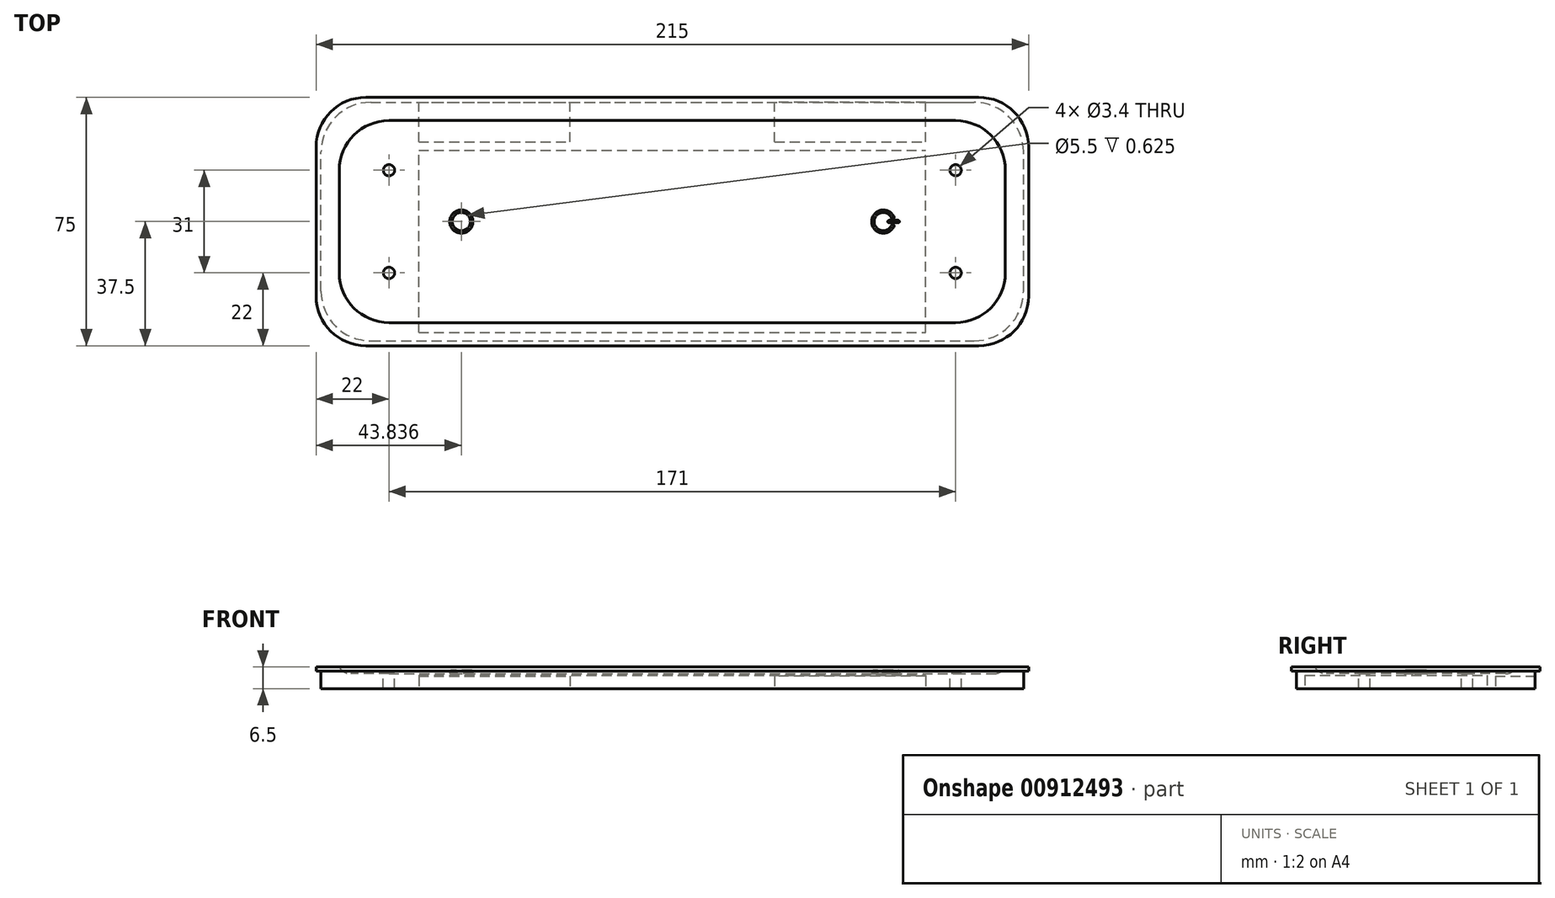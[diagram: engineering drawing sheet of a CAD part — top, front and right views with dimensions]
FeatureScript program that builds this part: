
annotation { "Feature Type Name" : "Feature", "Feature Type Description" : "" }
export const myFeature = defineFeature(function(context is Context, id is Id, definition is map)
    precondition{}
    {
        {
            var Q0;
            Q0=qCreatedBy(makeId("Top.planeOp"),FACE);
            var sketch = newSketch(context, id + "F0", { "sketchPlane" : qUnion([Q0])});
            skLineSegment(sketch, "E0.bottom", {"start": v(-107.5, 37.5) * mm, "end": v(107.5, 37.5) * mm});
            skLineSegment(sketch, "E0.top", {"start": v(-107.5, -37.5) * mm, "end": v(107.5, -37.5) * mm});
            skLineSegment(sketch, "E0.left", {"start": v(-107.5, 37.5) * mm, "end": v(-107.5, -37.5) * mm});
            skLineSegment(sketch, "E0.right", {"start": v(107.5, 37.5) * mm, "end": v(107.5, -37.5) * mm});
            skPoint(sketch, "E0.middle", {"position": v(0, 0) * mm});
            skSolve(sketch);
        }
        {
            var Q0;
            Q0=qSketchRegion(id+"F0",true);
            extrude(context, id + "F1", {"entities" : qUnion([Q0]), "depth" : 1.25 * mm, "offsetDistance" : 25 * mm});
        }
        {
            var Q0;
            Q0=makeQuery(id+"F1.opExtrude","SWEPT_EDGE",EDGE,{"disambiguationData":[OSD([sQuery(id+"F0.wireOp",EDGE,"E0.top"),sQuery(id+"F0.wireOp",EDGE,"E0.right")])]});
            var Q1;
            Q1=makeQuery(id+"F1.opExtrude","SWEPT_EDGE",EDGE,{"disambiguationData":[OSD([sQuery(id+"F0.wireOp",EDGE,"E0.bottom"),sQuery(id+"F0.wireOp",EDGE,"E0.right")])]});
            var Q2;
            Q2=makeQuery(id+"F1.opExtrude","SWEPT_EDGE",EDGE,{"disambiguationData":[OSD([sQuery(id+"F0.wireOp",EDGE,"E0.bottom"),sQuery(id+"F0.wireOp",EDGE,"E0.left")])]});
            var Q3;
            Q3=makeQuery(id+"F1.opExtrude","SWEPT_EDGE",EDGE,{"disambiguationData":[OSD([sQuery(id+"F0.wireOp",EDGE,"E0.top"),sQuery(id+"F0.wireOp",EDGE,"E0.left")])]});
            fillet(context, id + "F2", {"entities" : qUnion([Q0, Q1, Q2, Q3]), "radius" : 15 * mm, "tangentPropagation" : true, "allowEdgeOverflow" : false});
        }
        {
            var Q0;
            Q0=makeQuery(id+"F1.opExtrude","CAP_FACE",FACE,{"disambiguationData":[OSD([sQuery(id+"F0.wireOp",EDGE,"E0.bottom"),sQuery(id+"F0.wireOp",EDGE,"E0.top"),sQuery(id+"F0.wireOp",EDGE,"E0.left"),sQuery(id+"F0.wireOp",EDGE,"E0.right")])],"isStart":true});
            var sketch = newSketch(context, id + "F3", { "sketchPlane" : qUnion([Q0])});
            skLineSegment(sketch, "E1.bottom", {"start": v(-106, 36) * mm, "end": v(106, 36) * mm});
            skLineSegment(sketch, "E1.top", {"start": v(-106, -36) * mm, "end": v(106, -36) * mm});
            skLineSegment(sketch, "E1.left", {"start": v(-106, 36) * mm, "end": v(-106, -36) * mm});
            skLineSegment(sketch, "E1.right", {"start": v(106, 36) * mm, "end": v(106, -36) * mm});
            skPoint(sketch, "E1.middle", {"position": v(0, 0) * mm});
            skSolve(sketch);
        }
        {
            var Q0;
            Q0=qSketchRegion(id+"F3",true);
            extrude(context, id + "F4", {"entities" : qUnion([Q0]), "operationType" : NewBodyOperationType.ADD, "depth" : 5.25 * mm, "offsetDistance" : 25 * mm});
        }
        {
            var Q0;
            Q0=makeQuery(id+"F4.opExtrude","SWEPT_EDGE",EDGE,{"disambiguationData":[OSD([sQuery(id+"F3.wireOp",EDGE,"E1.bottom"),sQuery(id+"F3.wireOp",EDGE,"E1.left")])]});
            var Q1;
            Q1=makeQuery(id+"F4.opExtrude","SWEPT_EDGE",EDGE,{"disambiguationData":[OSD([sQuery(id+"F3.wireOp",EDGE,"E1.top"),sQuery(id+"F3.wireOp",EDGE,"E1.left")])]});
            var Q2;
            Q2=makeQuery(id+"F4.opExtrude","SWEPT_EDGE",EDGE,{"disambiguationData":[OSD([sQuery(id+"F3.wireOp",EDGE,"E1.top"),sQuery(id+"F3.wireOp",EDGE,"E1.right")])]});
            var Q3;
            Q3=makeQuery(id+"F4.opExtrude","SWEPT_EDGE",EDGE,{"disambiguationData":[OSD([sQuery(id+"F3.wireOp",EDGE,"E1.bottom"),sQuery(id+"F3.wireOp",EDGE,"E1.right")])]});
            fillet(context, id + "F5", {"entities" : qUnion([Q0, Q1, Q2, Q3]), "radius" : 15 * mm, "tangentPropagation" : true, "allowEdgeOverflow" : false});
        }
        {
            var Q0;
            Q0=makeQuery(id+"F1.opExtrude","CAP_FACE",FACE,{"disambiguationData":[OSD([sQuery(id+"F0.wireOp",EDGE,"E0.bottom"),sQuery(id+"F0.wireOp",EDGE,"E0.top"),sQuery(id+"F0.wireOp",EDGE,"E0.left"),sQuery(id+"F0.wireOp",EDGE,"E0.right")])],"isStart":false});
            var sketch = newSketch(context, id + "F6", { "sketchPlane" : qUnion([Q0])});
            skLineSegment(sketch, "E2.bottom", {"start": v(-106, 36) * mm, "end": v(106, 36) * mm});
            skLineSegment(sketch, "E2.top", {"start": v(-106, -36) * mm, "end": v(106, -36) * mm});
            skLineSegment(sketch, "E2.left", {"start": v(-106, 36) * mm, "end": v(-106, -36) * mm});
            skLineSegment(sketch, "E2.right", {"start": v(106, 36) * mm, "end": v(106, -36) * mm});
            skPoint(sketch, "E2.middle", {"position": v(0, 0) * mm});
            skSolve(sketch);
        }
        {
            var Q0;
            Q0=makeQuery(id+"F6.imprint","IMPRINT",FACE,{"disambiguationData":[TD([[makeQuery(id+"F6.imprint","IMPRINT",EDGE,{"derivedFrom":sQuery(id+"F6.wireOp",EDGE,"E2.bottom")}),-1.0]])]});
            var sketch = newSketch(context, id + "F7", { "sketchPlane" : qUnion([Q0])});
            skLineSegment(sketch, "E3.bottom", {"start": v(-100.5, 30.5) * mm, "end": v(100.5, 30.5) * mm});
            skLineSegment(sketch, "E3.top", {"start": v(-100.5, -30.5) * mm, "end": v(100.5, -30.5) * mm});
            skLineSegment(sketch, "E3.left", {"start": v(-100.5, 30.5) * mm, "end": v(-100.5, -30.5) * mm});
            skLineSegment(sketch, "E3.right", {"start": v(100.5, 30.5) * mm, "end": v(100.5, -30.5) * mm});
            skPoint(sketch, "E3.middle", {"position": v(0, 0) * mm});
            skSolve(sketch);
        }
        {
            var Q0;
            Q0=qSketchRegion(id+"F7",true);
            extrude(context, id + "F8", {"entities" : qUnion([Q0]), "operationType" : NewBodyOperationType.REMOVE, "oppositeDirection" : true, "depth" : 2 * mm, "offsetDistance" : 25 * mm});
        }
        {
            var Q0;
            Q0=makeQuery(id+"F8.boolean.opBoolean","COPY",EDGE,{"derivedFrom":makeQuery(id+"F8.opExtrude","SWEPT_EDGE",EDGE,{"disambiguationData":[OSD([sQuery(id+"F7.wireOp",EDGE,"E3.bottom"),sQuery(id+"F7.wireOp",EDGE,"E3.left")])]})});
            var Q1;
            Q1=makeQuery(id+"F8.boolean.opBoolean","COPY",EDGE,{"derivedFrom":makeQuery(id+"F8.opExtrude","SWEPT_EDGE",EDGE,{"disambiguationData":[OSD([sQuery(id+"F7.wireOp",EDGE,"E3.top"),sQuery(id+"F7.wireOp",EDGE,"E3.left")])]})});
            var Q2;
            Q2=makeQuery(id+"F8.boolean.opBoolean","COPY",EDGE,{"derivedFrom":makeQuery(id+"F8.opExtrude","SWEPT_EDGE",EDGE,{"disambiguationData":[OSD([sQuery(id+"F7.wireOp",EDGE,"E3.bottom"),sQuery(id+"F7.wireOp",EDGE,"E3.right")])]})});
            var Q3;
            Q3=makeQuery(id+"F8.boolean.opBoolean","COPY",EDGE,{"derivedFrom":makeQuery(id+"F8.opExtrude","SWEPT_EDGE",EDGE,{"disambiguationData":[OSD([sQuery(id+"F7.wireOp",EDGE,"E3.top"),sQuery(id+"F7.wireOp",EDGE,"E3.right")])]})});
            fillet(context, id + "F9", {"entities" : qUnion([Q0, Q1, Q2, Q3]), "radius" : 15 * mm, "tangentPropagation" : true, "allowEdgeOverflow" : false});
        }
        {
            var Q0;
            Q0=makeQuery(id+"F8.boolean.opBoolean","COPY",EDGE,{"derivedFrom":makeQuery(id+"F8.opExtrude","CAP_EDGE",EDGE,{"disambiguationData":[OSD([sQuery(id+"F7.wireOp",EDGE,"E3.left")])],"isStart":false})});
            fillet(context, id + "F10", {"entities" : qUnion([Q0]), "radius" : 4 * mm, "tangentPropagation" : true, "allowEdgeOverflow" : false});
        }
        {
            var Q0;
            Q0=makeQuery(id+"F4.opExtrude","SWEPT_FACE",FACE,{"disambiguationData":[OSD([sQuery(id+"F3.wireOp",EDGE,"E1.top")])]});
            var sketch = newSketch(context, id + "F11", { "sketchPlane" : qUnion([Q0])});
            skLineSegment(sketch, "E4.bottom", {"start": v(-76.5, -1.5) * mm, "end": v(-30.88, -1.5) * mm});
            skLineSegment(sketch, "E4.top", {"start": v(-76.5, -5.25) * mm, "end": v(-30.88, -5.25) * mm});
            skLineSegment(sketch, "E4.left", {"start": v(-76.5, -1.5) * mm, "end": v(-76.5, -5.25) * mm});
            skLineSegment(sketch, "E4.right", {"start": v(-30.88, -1.5) * mm, "end": v(-30.88, -5.25) * mm});
            skLineSegment(sketch, "E5.bottom", {"start": v(76.5, -1.5) * mm, "end": v(30.88, -1.5) * mm});
            skLineSegment(sketch, "E5.top", {"start": v(76.5, -5.25) * mm, "end": v(30.88, -5.25) * mm});
            skLineSegment(sketch, "E5.left", {"start": v(76.5, -1.5) * mm, "end": v(76.5, -5.25) * mm});
            skLineSegment(sketch, "E5.right", {"start": v(30.88, -1.5) * mm, "end": v(30.88, -5.25) * mm});
            skSolve(sketch);
        }
        {
            var Q0;
            Q0=qSketchRegion(id+"F11",true);
            extrude(context, id + "F12", {"entities" : qUnion([Q0]), "operationType" : NewBodyOperationType.REMOVE, "oppositeDirection" : true, "depth" : 12 * mm, "offsetDistance" : 25 * mm});
        }
        {
            var Q0;
            Q0=makeQuery(id+"F4.opExtrude","CAP_FACE",FACE,{"disambiguationData":[OSD([sQuery(id+"F3.wireOp",EDGE,"E1.bottom"),sQuery(id+"F3.wireOp",EDGE,"E1.top"),sQuery(id+"F3.wireOp",EDGE,"E1.left"),sQuery(id+"F3.wireOp",EDGE,"E1.right")])],"isStart":false});
            var sketch = newSketch(context, id + "F13", { "sketchPlane" : qUnion([Q0])});
            skLineSegment(sketch, "E6.bottom", {"start": v(-76.5, 33.5) * mm, "end": v(76.5, 33.5) * mm});
            skLineSegment(sketch, "E6.top", {"start": v(-76.5, -21.5) * mm, "end": v(76.5, -21.5) * mm});
            skLineSegment(sketch, "E6.left", {"start": v(-76.5, 33.5) * mm, "end": v(-76.5, -21.5) * mm});
            skLineSegment(sketch, "E6.right", {"start": v(76.5, 33.5) * mm, "end": v(76.5, -21.5) * mm});
            skPoint(sketch, "E6.middle", {"position": v(0, 0) * mm});
            skSolve(sketch);
        }
        {
            var Q0;
            Q0=qSketchRegion(id+"F13",true);
            extrude(context, id + "F14", {"entities" : qUnion([Q0]), "operationType" : NewBodyOperationType.REMOVE, "oppositeDirection" : true, "depth" : 4 * mm, "offsetDistance" : 25 * mm});
        }
        {
            var Q0;
            {var subQ1=sQuery(id+"F0.wireOp",EDGE,"E0.right");var subQ2=sQuery(id+"F0.wireOp",EDGE,"E0.left");var subQ3=sQuery(id+"F0.wireOp",EDGE,"E0.top");var subQ4=sQuery(id+"F0.wireOp",EDGE,"E0.bottom");var subQ5=makeQuery(id+"F1.opExtrude","CAP_FACE",FACE,{"disambiguationData":[OSD([subQ4,subQ3,subQ2,subQ1])],"isStart":false});var subQ10=sQuery(id+"F6.wireOp",EDGE,"E2.bottom");var subQ13=makeQuery(id+"F2.opFillet","BLEND_EDGE",EDGE,{"blendedFrom":[makeQuery(id+"F1.opExtrude","SWEPT_EDGE",EDGE,{"disambiguationData":[OSD([subQ4,subQ2])]}),subQ5],"blendedInto":[subQ5]});var subQ17=makeQuery(id+"F6.imprint","INTERSECT",VERTEX,{"derivedFrom":[subQ13,subQ10]});Q0=makeQuery(id+"F6.imprint","IMPRINT",FACE,{"disambiguationData":[TD([[makeQuery(id+"F6.imprint","IMPRINT",EDGE,{"disambiguationData":[TD([[subQ17,-1.0]])],"derivedFrom":subQ10}),-1.0]])]});}
            var sketch = newSketch(context, id + "F15", { "sketchPlane" : qUnion([Q0])});
            skPoint(sketch, "E7", {"position": v(-85.5, 15.5) * mm});
            skPoint(sketch, "E8", {"position": v(-85.5, -15.5) * mm});
            skPoint(sketch, "E9", {"position": v(85.5, 15.5) * mm});
            skPoint(sketch, "E10", {"position": v(85.5, -15.5) * mm});
            skSolve(sketch);
        }
        {
            var Q0;
            Q0=sQuery(id+"F15.wireOp",VERTEX,"E7");
            var Q1;
            Q1=sQuery(id+"F15.wireOp",VERTEX,"E8");
            var Q2;
            Q2=sQuery(id+"F15.wireOp",VERTEX,"E9");
            var Q3;
            Q3=sQuery(id+"F15.wireOp",VERTEX,"E10");
            var Q4;
            Q4=makeQuery(id+"F1.opExtrude","SWEPT_BODY",BODY,{"disambiguationData":[OSD([sQuery(id+"F0.wireOp",EDGE,"E0.bottom"),sQuery(id+"F0.wireOp",EDGE,"E0.top"),sQuery(id+"F0.wireOp",EDGE,"E0.left"),sQuery(id+"F0.wireOp",EDGE,"E0.right")])]});
            hole(context, id + "F16", {"style" : HoleStyle.SIMPLE, "endStyle" : HoleEndStyle.THROUGH, "standardTappedOrClearance" : lookupTablePath({ "fit" : "Normal", "standard" : "ISO", "size" : "M3", "type" : "Clearance" }), "standardBlindInLast" : lookupTablePath({ "fit" : "Normal", "standard" : "ISO", "size" : "M3", "type" : "Clearance" }), "holeDiameter" : 3.4 * mm, "majorDiameter" : 5 * mm, "isTappedThrough" : true, "tappedDepth" : 12 * mm, "tapClearance" : 3, "locations" : qUnion([Q0, Q1, Q2, Q3]), "scope" : qUnion([Q4])});
        }
        {
            var Q0;
            Q0=makeQuery(id+"F14.boolean.opBoolean","COPY",FACE,{"derivedFrom":makeQuery(id+"F14.opExtrude","CAP_FACE",FACE,{"disambiguationData":[OSD([sQuery(id+"F13.wireOp",EDGE,"E6.bottom"),sQuery(id+"F13.wireOp",EDGE,"E6.top"),sQuery(id+"F13.wireOp",EDGE,"E6.left"),sQuery(id+"F13.wireOp",EDGE,"E6.right")])],"isStart":false})});
            var sketch = newSketch(context, id + "F17", { "sketchPlane" : qUnion([Q0])});
            skCircle(sketch, "E11", {"center": v(-63.66, 0) * mm, "radius": 2.75 * mm});
            skCircle(sketch, "E12", {"center": v(-63.66, 0) * mm, "radius": 3.5 * mm});
            skArc(sketch, "E13", {"start": v(67.02, 1) * mm, "mid": v(60.16, 0) * mm, "end": v(67.02, -0.98) * mm});
            skArc(sketch, "E14", {"start": v(66.3, 0.79) * mm, "mid": v(60.91, 0) * mm, "end": v(66.3, -0.79) * mm});
            skLineSegment(sketch, "E15", {"start": v(66.3, 0.79) * mm, "end": v(67.02, 1) * mm});
            skLineSegment(sketch, "E16", {"start": v(66.3, -0.79) * mm, "end": v(67.02, -0.98) * mm});
            skLineSegment(sketch, "E17.bottom", {"start": v(65.04, 0.37) * mm, "end": v(68.54, 0.37) * mm});
            skLineSegment(sketch, "E17.top", {"start": v(65.04, -0.37) * mm, "end": v(68.54, -0.37) * mm});
            skLineSegment(sketch, "E17.left", {"start": v(65.04, 0.37) * mm, "end": v(65.04, -0.38) * mm});
            skLineSegment(sketch, "E17.right", {"start": v(68.54, 0.37) * mm, "end": v(68.54, -0.38) * mm});
            skSolve(sketch);
        }
        {
            var Q0;
            Q0 = qSketchRegion(id + "F17", true);
            extrude(context, id + "F18", {"entities" : qUnion([Q0]), "operationType" : NewBodyOperationType.ADD, "oppositeDirection" : true, "depth" : 1.5 * mm, "offsetDistance" : 25 * mm});
        }
        {
            var Q0;
            Q0=makeQuery(id+"F18.opExtrude","CAP_EDGE",EDGE,{"disambiguationData":[OSD([sQuery(id+"F17.wireOp",EDGE,"E11")])],"isStart":false});
            var Q1;
            Q1=makeQuery(id+"F18.opExtrude","CAP_EDGE",EDGE,{"disambiguationData":[OSD([sQuery(id+"F17.wireOp",EDGE,"E12")])],"isStart":false});
            var Q2;
            Q2=makeQuery(id+"F18.opExtrude","CAP_EDGE",EDGE,{"disambiguationData":[OSD([sQuery(id+"F17.wireOp",EDGE,"E14")])],"isStart":false});
            var Q3;
            Q3=makeQuery(id+"F18.opExtrude","CAP_EDGE",EDGE,{"disambiguationData":[OSD([sQuery(id+"F17.wireOp",EDGE,"E13")])],"isStart":false});
            var Q4;
            Q4=makeQuery(id+"F18.opExtrude","SWEPT_EDGE",EDGE,{"disambiguationData":[OSD([sQuery(id+"F17.wireOp",EDGE,"E13"),sQuery(id+"F17.wireOp",EDGE,"E15")])]});
            var Q5;
            Q5=makeQuery(id+"F18.opExtrude","CAP_EDGE",EDGE,{"disambiguationData":[OSD([sQuery(id+"F17.wireOp",EDGE,"E15")])],"isStart":false});
            var Q6;
            Q6=makeQuery(id+"F18.opExtrude","SWEPT_EDGE",EDGE,{"disambiguationData":[OSD([sQuery(id+"F17.wireOp",EDGE,"E14"),sQuery(id+"F17.wireOp",EDGE,"E15")])]});
            var Q7;
            Q7=makeQuery(id+"F18.opExtrude","CAP_EDGE",EDGE,{"disambiguationData":[OSD([sQuery(id+"F17.wireOp",EDGE,"E16")])],"isStart":false});
            var Q8;
            Q8=makeQuery(id+"F18.opExtrude","SWEPT_EDGE",EDGE,{"disambiguationData":[OSD([sQuery(id+"F17.wireOp",EDGE,"E14"),sQuery(id+"F17.wireOp",EDGE,"E16")])]});
            var Q9;
            Q9=makeQuery(id+"F18.opExtrude","SWEPT_EDGE",EDGE,{"disambiguationData":[OSD([sQuery(id+"F17.wireOp",EDGE,"E13"),sQuery(id+"F17.wireOp",EDGE,"E16")])]});
            var Q10;
            Q10=makeQuery(id+"F18.opExtrude","CAP_EDGE",EDGE,{"disambiguationData":[OSD([sQuery(id+"F17.wireOp",EDGE,"E17.left")])],"isStart":false});
            var Q11;
            Q11=makeQuery(id+"F18.opExtrude","SWEPT_EDGE",EDGE,{"disambiguationData":[OSD([sQuery(id+"F17.wireOp",EDGE,"E17.bottom"),sQuery(id+"F17.wireOp",EDGE,"E17.left")])]});
            var Q12;
            Q12=makeQuery(id+"F18.opExtrude","SWEPT_EDGE",EDGE,{"disambiguationData":[OSD([sQuery(id+"F17.wireOp",EDGE,"E17.top"),sQuery(id+"F17.wireOp",EDGE,"E17.left")])]});
            var Q13;
            Q13=makeQuery(id+"F18.opExtrude","CAP_EDGE",EDGE,{"disambiguationData":[OSD([sQuery(id+"F17.wireOp",EDGE,"E17.bottom")])],"isStart":false});
            var Q14;
            Q14=makeQuery(id+"F18.opExtrude","CAP_EDGE",EDGE,{"disambiguationData":[OSD([sQuery(id+"F17.wireOp",EDGE,"E17.top")])],"isStart":false});
            var Q15;
            Q15=makeQuery(id+"F18.opExtrude","SWEPT_EDGE",EDGE,{"disambiguationData":[OSD([sQuery(id+"F17.wireOp",EDGE,"E17.bottom"),sQuery(id+"F17.wireOp",EDGE,"E17.right")])]});
            var Q16;
            Q16=makeQuery(id+"F18.opExtrude","SWEPT_EDGE",EDGE,{"disambiguationData":[OSD([sQuery(id+"F17.wireOp",EDGE,"E17.top"),sQuery(id+"F17.wireOp",EDGE,"E17.right")])]});
            var Q17;
            Q17=makeQuery(id+"F18.opExtrude","CAP_EDGE",EDGE,{"disambiguationData":[OSD([sQuery(id+"F17.wireOp",EDGE,"E17.right")])],"isStart":false});
            fillet(context, id + "F19", {"entities" : qUnion([Q0, Q1, Q2, Q3, Q4, Q5, Q6, Q7, Q8, Q9, Q10, Q11, Q12, Q13, Q14, Q15, Q16, Q17]), "radius" : 0.38 * mm, "tangentPropagation" : true, "allowEdgeOverflow" : false});
        }
    });
